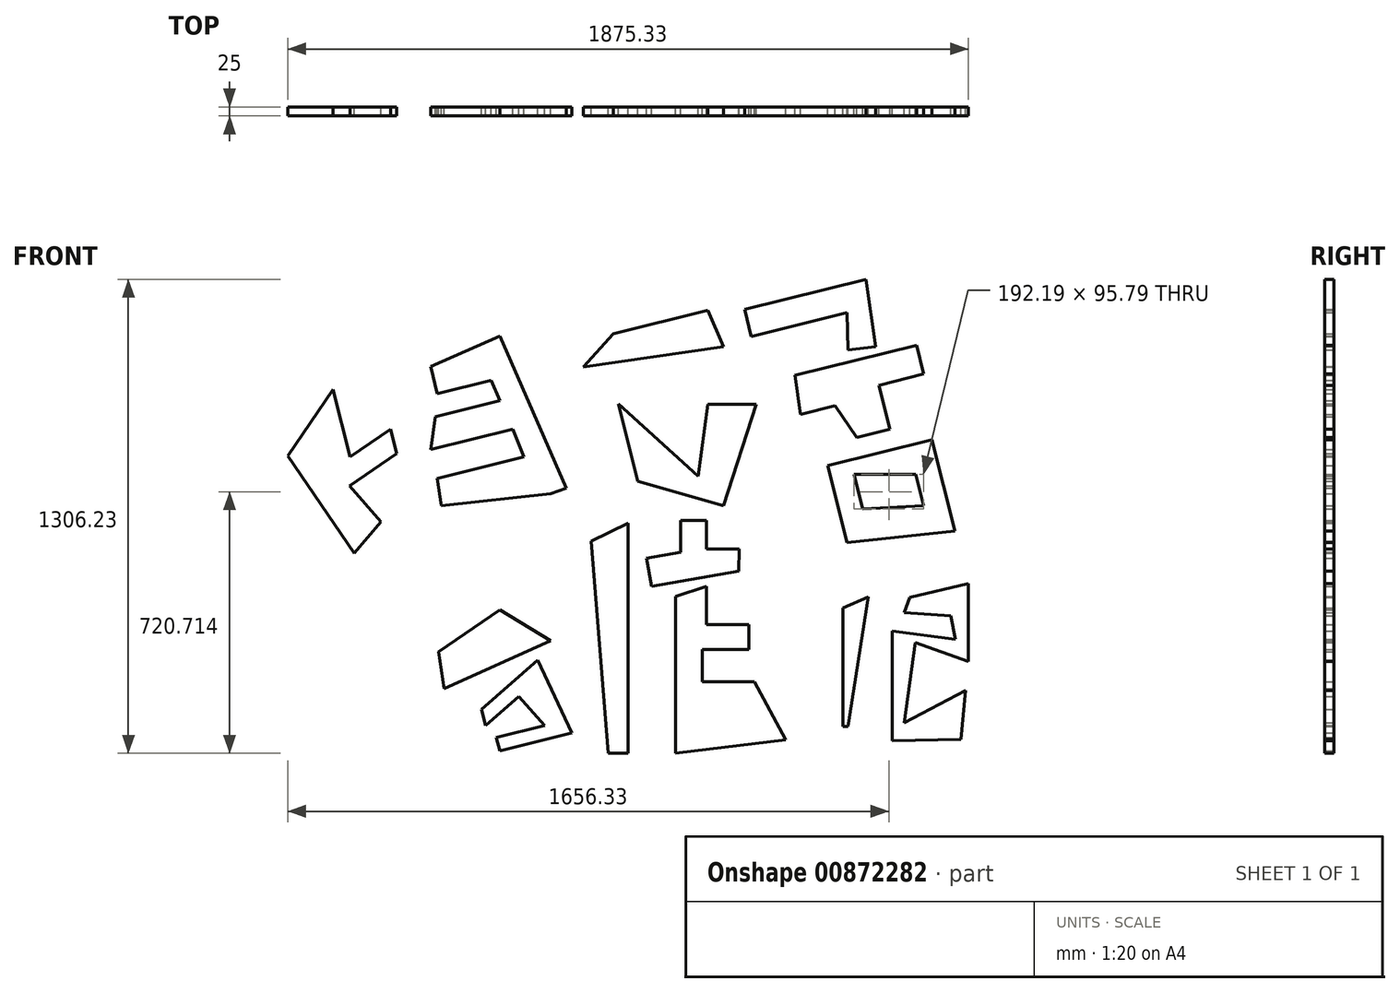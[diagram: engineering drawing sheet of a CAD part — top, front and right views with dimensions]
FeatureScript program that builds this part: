
annotation { "Feature Type Name" : "Feature", "Feature Type Description" : "" }
export const myFeature = defineFeature(function(context is Context, id is Id, definition is map)
    precondition{}
    {
        {
            var Q0;
            Q0=qCreatedBy(makeId("Front.planeOp"),FACE);
            var sketch = newSketch(context, id + "F0", { "sketchPlane" : qUnion([Q0])});
            skLineSegment(sketch, "E0", {"start": v(294.23, -290.17) * mm, "end": v(307.89, -155.16) * mm});
            skLineSegment(sketch, "E1", {"start": v(307.89, -155.16) * mm, "end": v(137.97, -244) * mm});
            skLineSegment(sketch, "E2", {"start": v(137.97, -244) * mm, "end": v(168.58, -23.15) * mm});
            skLineSegment(sketch, "E3", {"start": v(168.58, -23.15) * mm, "end": v(315.1, -74.79) * mm});
            skLineSegment(sketch, "E4", {"start": v(315.1, -74.79) * mm, "end": v(315.1, 139.43) * mm});
            skLineSegment(sketch, "E5", {"start": v(315.1, 139.43) * mm, "end": v(153.64, 101.84) * mm});
            skLineSegment(sketch, "E6", {"start": v(153.64, 101.84) * mm, "end": v(138.28, 59.16) * mm});
            skLineSegment(sketch, "E7", {"start": v(138.28, 59.16) * mm, "end": v(267, 49.87) * mm});
            skLineSegment(sketch, "E8", {"start": v(267, 49.87) * mm, "end": v(278.94, -14) * mm});
            skLineSegment(sketch, "E9", {"start": v(278.94, -14) * mm, "end": v(105.62, 9) * mm});
            skLineSegment(sketch, "E10", {"start": v(105.62, 9) * mm, "end": v(105.62, -293.16) * mm});
            skLineSegment(sketch, "E11", {"start": v(105.62, -293.16) * mm, "end": v(294.23, -290.17) * mm});
            skLineSegment(sketch, "E12", {"start": v(-16.64, -254.22) * mm, "end": v(39.65, 102.28) * mm});
            skLineSegment(sketch, "E13", {"start": v(39.65, 102.28) * mm, "end": v(-30.6, 71.57) * mm});
            skLineSegment(sketch, "E14", {"start": v(-30.6, 71.57) * mm, "end": v(-30.6, -254.4) * mm});
            skLineSegment(sketch, "E15", {"start": v(-30.6, -254.4) * mm, "end": v(-16.64, -254.22) * mm});
            skLineSegment(sketch, "E16", {"start": v(-975.93, -321.59) * mm, "end": v(-777.35, -271.96) * mm});
            skLineSegment(sketch, "E17", {"start": v(-777.35, -271.96) * mm, "end": v(-871.87, -71.24) * mm});
            skLineSegment(sketch, "E18", {"start": v(-871.87, -71.24) * mm, "end": v(-1025.58, -206.99) * mm});
            skLineSegment(sketch, "E19", {"start": v(-1025.58, -206.99) * mm, "end": v(-1014.33, -251.99) * mm});
            skLineSegment(sketch, "E20", {"start": v(-1014.33, -251.99) * mm, "end": v(-923.54, -171.24) * mm});
            skLineSegment(sketch, "E21", {"start": v(-923.54, -171.24) * mm, "end": v(-851.73, -251.99) * mm});
            skLineSegment(sketch, "E22", {"start": v(-851.73, -251.99) * mm, "end": v(-985.45, -285.4) * mm});
            skLineSegment(sketch, "E23", {"start": v(-985.45, -285.4) * mm, "end": v(-975.93, -321.59) * mm});
            skLineSegment(sketch, "E24", {"start": v(-835.85, -17.89) * mm, "end": v(-1129.23, -150.5) * mm});
            skLineSegment(sketch, "E25", {"start": v(-1129.23, -150.5) * mm, "end": v(-1144.08, -48.46) * mm});
            skLineSegment(sketch, "E26", {"start": v(-1144.08, -48.46) * mm, "end": v(-975.93, 66.9) * mm});
            skLineSegment(sketch, "E27", {"start": v(-975.93, 66.9) * mm, "end": v(-835.85, -17.89) * mm});
            skLineSegment(sketch, "E28", {"start": v(277.85, 283.65) * mm, "end": v(214.74, 536.15) * mm});
            skLineSegment(sketch, "E29", {"start": v(214.74, 536.15) * mm, "end": v(-71.92, 464.5) * mm});
            skLineSegment(sketch, "E30", {"start": v(-71.92, 464.5) * mm, "end": v(-18.8, 251.95) * mm});
            skLineSegment(sketch, "E31", {"start": v(-18.8, 251.95) * mm, "end": v(277.85, 283.65) * mm});
            skLineSegment(sketch, "E32", {"start": v(192.2, 354.28) * mm, "end": v(170.67, 440.4) * mm});
            skLineSegment(sketch, "E33", {"start": v(170.67, 440.4) * mm, "end": v(0, 440.4) * mm});
            skLineSegment(sketch, "E34", {"start": v(0, 440.4) * mm, "end": v(23.94, 344.61) * mm});
            skLineSegment(sketch, "E35", {"start": v(23.94, 344.61) * mm, "end": v(192.2, 354.28) * mm});
            skLineSegment(sketch, "E36", {"start": v(99.07, 565.16) * mm, "end": v(68.9, 685.85) * mm});
            skLineSegment(sketch, "E37", {"start": v(68.9, 685.85) * mm, "end": v(192.2, 716.66) * mm});
            skLineSegment(sketch, "E38", {"start": v(192.2, 716.66) * mm, "end": v(172.23, 796.56) * mm});
            skLineSegment(sketch, "E39", {"start": v(172.23, 796.56) * mm, "end": v(-162.84, 712.82) * mm});
            skLineSegment(sketch, "E40", {"start": v(-162.84, 712.82) * mm, "end": v(-147.23, 605.52) * mm});
            skLineSegment(sketch, "E41", {"start": v(-147.23, 605.52) * mm, "end": v(-51.96, 629.33) * mm});
            skLineSegment(sketch, "E42", {"start": v(-51.96, 629.33) * mm, "end": v(8.08, 541.82) * mm});
            skLineSegment(sketch, "E43", {"start": v(8.08, 541.82) * mm, "end": v(99.07, 565.16) * mm});
            skLineSegment(sketch, "E44", {"start": v(60.18, 792.26) * mm, "end": v(33.15, 978.02) * mm});
            skLineSegment(sketch, "E45", {"start": v(33.15, 978.02) * mm, "end": v(-301.33, 894.43) * mm});
            skLineSegment(sketch, "E46", {"start": v(-301.33, 894.43) * mm, "end": v(-282.68, 819.8) * mm});
            skLineSegment(sketch, "E47", {"start": v(-282.68, 819.8) * mm, "end": v(-18.8, 885.75) * mm});
            skLineSegment(sketch, "E48", {"start": v(-18.8, 885.75) * mm, "end": v(-16.14, 783.17) * mm});
            skLineSegment(sketch, "E49", {"start": v(-16.14, 783.17) * mm, "end": v(60.18, 792.26) * mm});
            skLineSegment(sketch, "E50", {"start": v(-359.05, 354.28) * mm, "end": v(-268.73, 633.8) * mm});
            skLineSegment(sketch, "E51", {"start": v(-268.73, 633.8) * mm, "end": v(-402.43, 633.8) * mm});
            skLineSegment(sketch, "E52", {"start": v(-402.43, 633.8) * mm, "end": v(-429.94, 435.35) * mm});
            skLineSegment(sketch, "E53", {"start": v(-429.94, 435.35) * mm, "end": v(-648.67, 634.34) * mm});
            skLineSegment(sketch, "E54", {"start": v(-648.67, 634.34) * mm, "end": v(-595.52, 421.69) * mm});
            skLineSegment(sketch, "E55", {"start": v(-595.52, 421.69) * mm, "end": v(-359.05, 354.28) * mm});
            skLineSegment(sketch, "E56", {"start": v(-359.05, 792.26) * mm, "end": v(-745.6, 736.01) * mm});
            skLineSegment(sketch, "E57", {"start": v(-745.6, 736.01) * mm, "end": v(-663.11, 827.98) * mm});
            skLineSegment(sketch, "E58", {"start": v(-663.11, 827.98) * mm, "end": v(-402.43, 893.13) * mm});
            skLineSegment(sketch, "E59", {"start": v(-402.43, 893.13) * mm, "end": v(-359.05, 792.26) * mm});
            skLineSegment(sketch, "E60", {"start": v(-835.85, 386.5) * mm, "end": v(-1137.35, 354.28) * mm});
            skLineSegment(sketch, "E61", {"start": v(-1137.35, 354.28) * mm, "end": v(-1148.24, 429.14) * mm});
            skLineSegment(sketch, "E62", {"start": v(-1148.24, 429.14) * mm, "end": v(-908.95, 488.94) * mm});
            skLineSegment(sketch, "E63", {"start": v(-908.95, 488.94) * mm, "end": v(-939.6, 565.16) * mm});
            skLineSegment(sketch, "E64", {"start": v(-939.6, 565.16) * mm, "end": v(-1166.23, 508.52) * mm});
            skLineSegment(sketch, "E65", {"start": v(-1166.23, 508.52) * mm, "end": v(-1153.73, 598.7) * mm});
            skLineSegment(sketch, "E66", {"start": v(-1153.73, 598.7) * mm, "end": v(-975.93, 643.14) * mm});
            skLineSegment(sketch, "E67", {"start": v(-975.93, 643.14) * mm, "end": v(-999.07, 699.78) * mm});
            skLineSegment(sketch, "E68", {"start": v(-999.07, 699.78) * mm, "end": v(-1147.66, 662.65) * mm});
            skLineSegment(sketch, "E69", {"start": v(-1147.66, 662.65) * mm, "end": v(-1166.46, 737.89) * mm});
            skLineSegment(sketch, "E70", {"start": v(-1166.46, 737.89) * mm, "end": v(-975.93, 821.1) * mm});
            skLineSegment(sketch, "E71", {"start": v(-975.93, 821.1) * mm, "end": v(-793.1, 402.47) * mm});
            skLineSegment(sketch, "E72", {"start": v(-793.1, 402.47) * mm, "end": v(-835.85, 386.5) * mm});
            skLineSegment(sketch, "E73", {"start": v(-1389.15, 408.31) * mm, "end": v(-1259.37, 497.35) * mm});
            skLineSegment(sketch, "E74", {"start": v(-1259.37, 497.35) * mm, "end": v(-1276.32, 565.16) * mm});
            skLineSegment(sketch, "E75", {"start": v(-1276.32, 565.16) * mm, "end": v(-1388.14, 488.44) * mm});
            skLineSegment(sketch, "E76", {"start": v(-1388.14, 488.44) * mm, "end": v(-1434.65, 674.57) * mm});
            skLineSegment(sketch, "E77", {"start": v(-1434.65, 674.57) * mm, "end": v(-1560.23, 490.65) * mm});
            skLineSegment(sketch, "E78", {"start": v(-1560.23, 490.65) * mm, "end": v(-1376.73, 223.19) * mm});
            skLineSegment(sketch, "E79", {"start": v(-1376.73, 223.19) * mm, "end": v(-1303.23, 309.76) * mm});
            skLineSegment(sketch, "E80", {"start": v(-1303.23, 309.76) * mm, "end": v(-1389.15, 408.31) * mm});
            skLineSegment(sketch, "E81", {"start": v(-187.44, -291.03) * mm, "end": v(-274.22, -130.69) * mm});
            skLineSegment(sketch, "E82", {"start": v(-274.22, -130.69) * mm, "end": v(-418.3, -130.69) * mm});
            skLineSegment(sketch, "E83", {"start": v(-418.3, -130.69) * mm, "end": v(-418.3, -42.15) * mm});
            skLineSegment(sketch, "E84", {"start": v(-418.3, -42.15) * mm, "end": v(-289.06, -42.15) * mm});
            skLineSegment(sketch, "E85", {"start": v(-289.06, -42.15) * mm, "end": v(-289.06, 26.43) * mm});
            skLineSegment(sketch, "E86", {"start": v(-289.06, 26.43) * mm, "end": v(-405.93, 26.43) * mm});
            skLineSegment(sketch, "E87", {"start": v(-405.93, 26.43) * mm, "end": v(-405.93, 132.17) * mm});
            skLineSegment(sketch, "E88", {"start": v(-405.93, 132.17) * mm, "end": v(-491.87, 104.14) * mm});
            skLineSegment(sketch, "E89", {"start": v(-491.87, 104.14) * mm, "end": v(-491.87, -328.21) * mm});
            skLineSegment(sketch, "E90", {"start": v(-491.87, -328.21) * mm, "end": v(-187.44, -291.03) * mm});
            skLineSegment(sketch, "E91", {"start": v(-317.47, 173.64) * mm, "end": v(-558.14, 132.17) * mm});
            skLineSegment(sketch, "E92", {"start": v(-558.14, 132.17) * mm, "end": v(-571.36, 208.93) * mm});
            skLineSegment(sketch, "E93", {"start": v(-571.36, 208.93) * mm, "end": v(-477.29, 225.14) * mm});
            skLineSegment(sketch, "E94", {"start": v(-477.29, 225.14) * mm, "end": v(-477.29, 313.9) * mm});
            skLineSegment(sketch, "E95", {"start": v(-477.29, 313.9) * mm, "end": v(-405.93, 313.9) * mm});
            skLineSegment(sketch, "E96", {"start": v(-405.93, 313.9) * mm, "end": v(-405.93, 234.69) * mm});
            skLineSegment(sketch, "E97", {"start": v(-405.93, 234.69) * mm, "end": v(-316.1, 234.69) * mm});
            skLineSegment(sketch, "E98", {"start": v(-316.1, 234.69) * mm, "end": v(-317.47, 173.64) * mm});
            skLineSegment(sketch, "E99", {"start": v(-621.82, -328.21) * mm, "end": v(-621.82, 306.01) * mm});
            skLineSegment(sketch, "E100", {"start": v(-621.82, 306.01) * mm, "end": v(-724.3, 256.59) * mm});
            skLineSegment(sketch, "E101", {"start": v(-724.3, 256.59) * mm, "end": v(-676.63, -328.21) * mm});
            skLineSegment(sketch, "E102", {"start": v(-676.63, -328.21) * mm, "end": v(-621.82, -328.21) * mm});
            skSolve(sketch);
        }
        {
            var Q0;
            Q0 = qSketchRegion(id + "F0", true);
            extrude(context, id + "F1", {"entities" : qUnion([Q0]), "depth" : 25 * mm, "offsetDistance" : 25 * mm});
        }
    });
